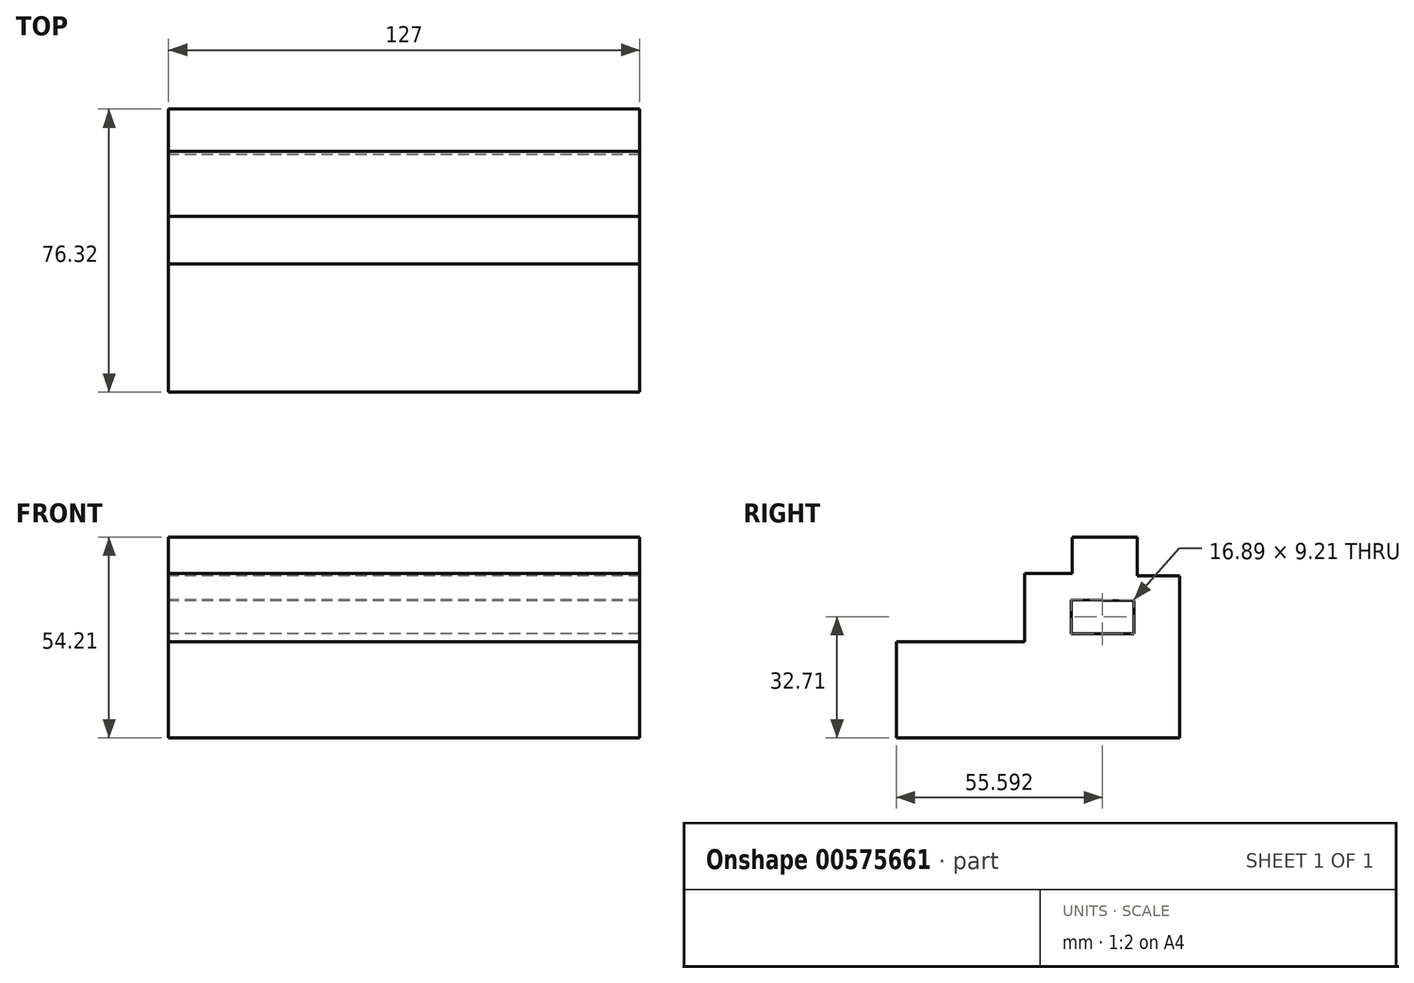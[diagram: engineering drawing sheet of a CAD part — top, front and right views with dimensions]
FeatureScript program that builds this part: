
annotation { "Feature Type Name" : "Feature", "Feature Type Description" : "" }
export const myFeature = defineFeature(function(context is Context, id is Id, definition is map)
    precondition{}
    {
        {
            var Q0;
            Q0=qCreatedBy(makeId("Right.planeOp"),FACE);
            var sketch = newSketch(context, id + "F0", { "sketchPlane" : qUnion([Q0])});
            skLineSegment(sketch, "E0", {"start": v(0, 0) * mm, "end": v(76.32, 0) * mm});
            skLineSegment(sketch, "E1", {"start": v(76.32, 0) * mm, "end": v(76.32, 43.77) * mm});
            skLineSegment(sketch, "E2", {"start": v(76.32, 43.77) * mm, "end": v(64.96, 43.77) * mm});
            skLineSegment(sketch, "E3", {"start": v(64.96, 43.77) * mm, "end": v(64.96, 54.21) * mm});
            skLineSegment(sketch, "E4", {"start": v(64.96, 54.21) * mm, "end": v(47.45, 54.21) * mm});
            skLineSegment(sketch, "E5", {"start": v(47.45, 54.21) * mm, "end": v(47.45, 44.38) * mm});
            skLineSegment(sketch, "E6", {"start": v(47.45, 44.38) * mm, "end": v(34.55, 44.38) * mm});
            skLineSegment(sketch, "E7", {"start": v(34.55, 44.38) * mm, "end": v(34.55, 25.95) * mm});
            skLineSegment(sketch, "E8", {"start": v(34.55, 25.95) * mm, "end": v(0, 25.95) * mm});
            skLineSegment(sketch, "E9", {"start": v(0, 25.95) * mm, "end": v(0, 0) * mm});
            skLineSegment(sketch, "E10", {"start": v(47.15, 37.32) * mm, "end": v(47.15, 28.1) * mm});
            skLineSegment(sketch, "E11", {"start": v(47.15, 28.1) * mm, "end": v(64.04, 28.1) * mm});
            skLineSegment(sketch, "E12", {"start": v(64.04, 28.1) * mm, "end": v(64.04, 37.01) * mm});
            skLineSegment(sketch, "E13", {"start": v(64.04, 37.01) * mm, "end": v(47.15, 37.32) * mm});
            skSolve(sketch);
        }
        {
            var Q0;
            Q0 = qSketchRegion(id + "F0", true);
            extrude(context, id + "F1", {"entities" : qUnion([Q0]), "depth" : 127 * mm, "offsetDistance" : 25.4 * mm});
        }
    });
